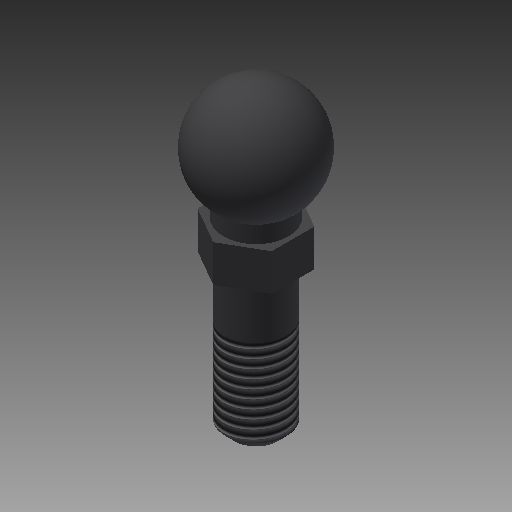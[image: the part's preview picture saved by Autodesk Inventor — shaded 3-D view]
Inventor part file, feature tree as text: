
AUTODESK INVENTOR PART (.ipt)
format: ipt  version: 2018 (Build 220112000, 112)  size: 157,696 bytes
history: native  units: mm
features: other x7, sketch x2, revolve x1, thread x1, extrude x1
ambient origin geometry x8: Origin, YZ Plane, XZ Plane, XY Plane, X Axis, Y Axis, Z Axis, Center Point
bodies: Solid1 (feature_tree)
feature tree (12):
  revolve  "Revolution1"  [1 undecoded]
  thread  "Thread1"  [1 undecoded]
  extrude  "Extrusion1"  [1 undecoded]
  other  "IP1_XY"
  other  "IP1_YZ"
  other  "IP1_ZX"
  other  "IP1_X"
  other  "IP1_Y"
  other  "IP1_Z"
  other  "IP1_Center"
  sketch  "Sketch_2"  dims[d0=360.0deg d1=20.0mm d2=0.0mm d3=8.5mm d4=0.0mm]
  sketch  "Sketch_3"
note: 3 required parameter values undecoded (feature->parameter linkage not recoverable at this tier; creation-order binding heuristic only, values carry confidence <= 0.55)